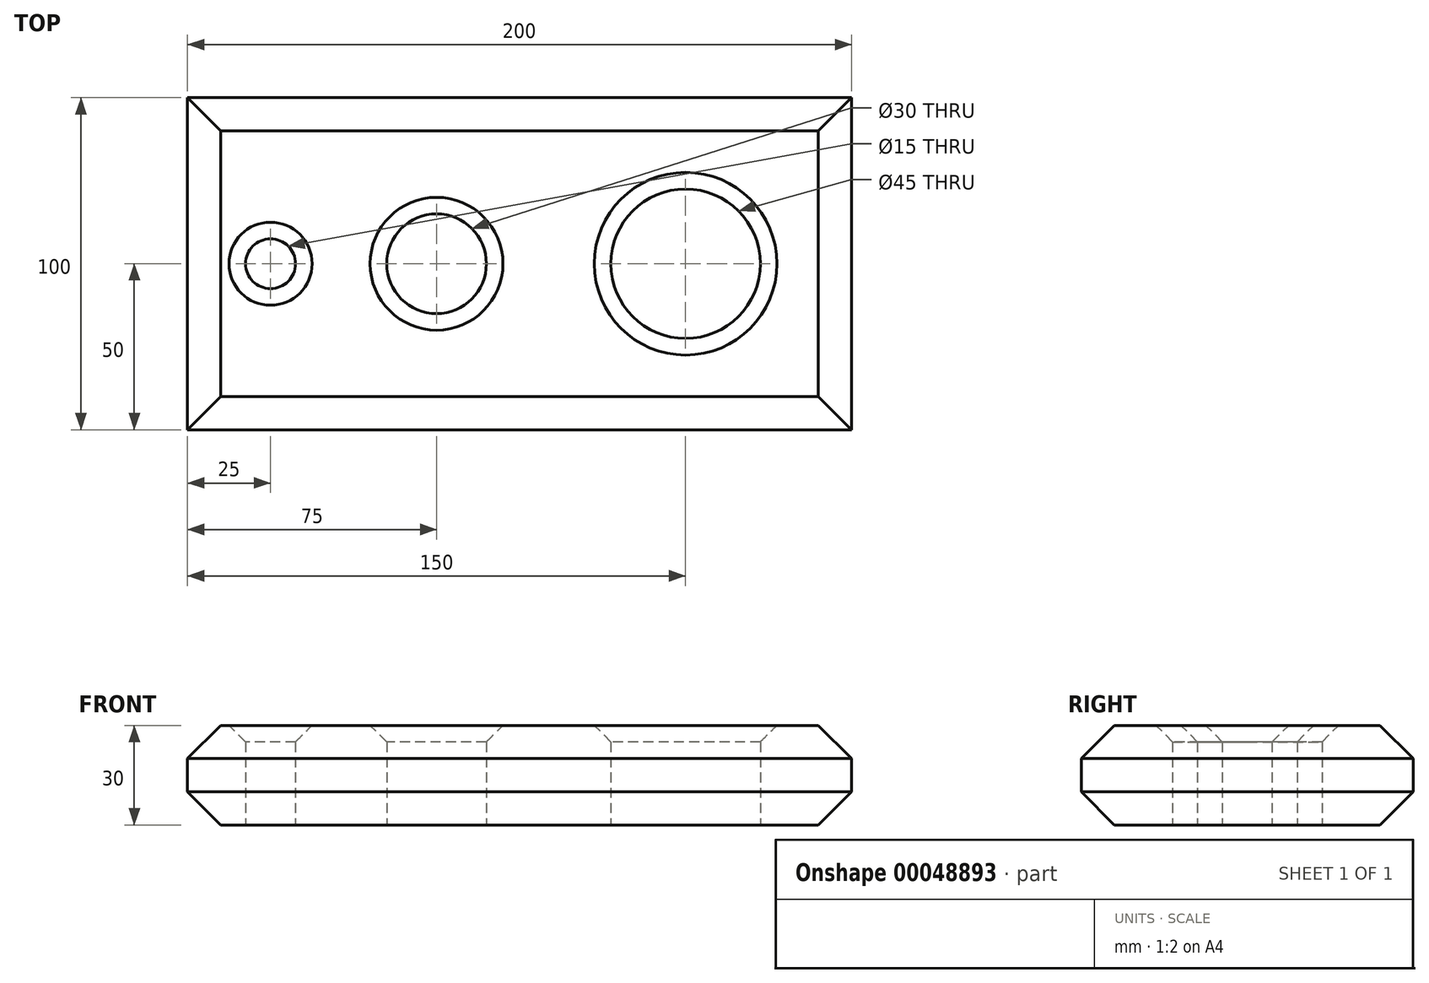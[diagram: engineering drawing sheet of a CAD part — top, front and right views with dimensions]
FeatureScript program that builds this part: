
annotation { "Feature Type Name" : "Feature", "Feature Type Description" : "" }
export const myFeature = defineFeature(function(context is Context, id is Id, definition is map)
    precondition{}
    {
        {
            var Q0;
            Q0=qCreatedBy(makeId("Top.planeOp"),FACE);
            var sketch = newSketch(context, id + "F0", { "sketchPlane" : qUnion([Q0])});
            skLineSegment(sketch, "E0.rect.bottom", {"start": v(100, 50) * mm, "end": v(-100, 50) * mm});
            skLineSegment(sketch, "E0.rect.top", {"start": v(100, -50) * mm, "end": v(-100, -50) * mm});
            skLineSegment(sketch, "E0.rect.left", {"start": v(100, 50) * mm, "end": v(100, -50) * mm});
            skLineSegment(sketch, "E0.rect.right", {"start": v(-100, 50) * mm, "end": v(-100, -50) * mm});
            skPoint(sketch, "E0.rect.middle", {"position": v(0, 0) * mm});
            skCircle(sketch, "E1", {"center": v(-75, 0) * mm, "radius": 7.5 * mm});
            skPoint(sketch, "E1.centerSnap0", {"position": v(-100, 0) * mm});
            skCircle(sketch, "E2", {"center": v(-25, 0) * mm, "radius": 15 * mm});
            skCircle(sketch, "E3", {"center": v(50, 0) * mm, "radius": 22.5 * mm});
            skSolve(sketch);
        }
        {
            var Q0;
            Q0=makeQuery(id+"F0.imprint","IMPRINT",FACE,{"disambiguationData":[TD([[makeQuery(id+"F0.imprint","IMPRINT",EDGE,{"derivedFrom":sQuery(id+"F0.wireOp",EDGE,"E0.rect.bottom")}),1.0]])]});
            extrude(context, id + "F1", {"entities" : qUnion([Q0]), "depth" : 30 * mm});
        }
        {
            var Q0;
            Q0=makeQuery(id+"F1.opExtrude","CAP_EDGE",EDGE,{"disambiguationData":[OSD([sQuery(id+"F0.wireOp",EDGE,"E0.rect.top")])],"isStart":false});
            var Q1;
            Q1=makeQuery(id+"F1.opExtrude","CAP_EDGE",EDGE,{"disambiguationData":[OSD([sQuery(id+"F0.wireOp",EDGE,"E0.rect.left")])],"isStart":false});
            var Q2;
            Q2=makeQuery(id+"F1.opExtrude","CAP_EDGE",EDGE,{"disambiguationData":[OSD([sQuery(id+"F0.wireOp",EDGE,"E0.rect.right")])],"isStart":false});
            var Q3;
            Q3=makeQuery(id+"F1.opExtrude","CAP_EDGE",EDGE,{"disambiguationData":[OSD([sQuery(id+"F0.wireOp",EDGE,"E0.rect.bottom")])],"isStart":false});
            var Q4;
            Q4=makeQuery(id+"F1.opExtrude","CAP_EDGE",EDGE,{"disambiguationData":[OSD([sQuery(id+"F0.wireOp",EDGE,"E0.rect.top")])],"isStart":true});
            var Q5;
            Q5=makeQuery(id+"F1.opExtrude","CAP_EDGE",EDGE,{"disambiguationData":[OSD([sQuery(id+"F0.wireOp",EDGE,"E0.rect.left")])],"isStart":true});
            var Q6;
            Q6=makeQuery(id+"F1.opExtrude","CAP_EDGE",EDGE,{"disambiguationData":[OSD([sQuery(id+"F0.wireOp",EDGE,"E0.rect.right")])],"isStart":true});
            var Q7;
            Q7=makeQuery(id+"F1.opExtrude","CAP_EDGE",EDGE,{"disambiguationData":[OSD([sQuery(id+"F0.wireOp",EDGE,"E0.rect.bottom")])],"isStart":true});
            chamfer(context, id + "F2", {"entities" : qUnion([Q0, Q1, Q2, Q3, Q4, Q5, Q6, Q7]), "width" : 10 * mm, "tangentPropagation" : true});
        }
        {
            var Q0;
            Q0=makeQuery(id+"F1.opExtrude","CAP_EDGE",EDGE,{"disambiguationData":[OSD([sQuery(id+"F0.wireOp",EDGE,"E3")])],"isStart":false});
            var Q1;
            Q1=makeQuery(id+"F1.opExtrude","CAP_EDGE",EDGE,{"disambiguationData":[OSD([sQuery(id+"F0.wireOp",EDGE,"E2")])],"isStart":false});
            var Q2;
            Q2=makeQuery(id+"F1.opExtrude","CAP_EDGE",EDGE,{"disambiguationData":[OSD([sQuery(id+"F0.wireOp",EDGE,"E1")])],"isStart":false});
            chamfer(context, id + "F3", {"entities" : qUnion([Q0, Q1, Q2]), "width" : 5 * mm, "tangentPropagation" : true});
        }
    });
